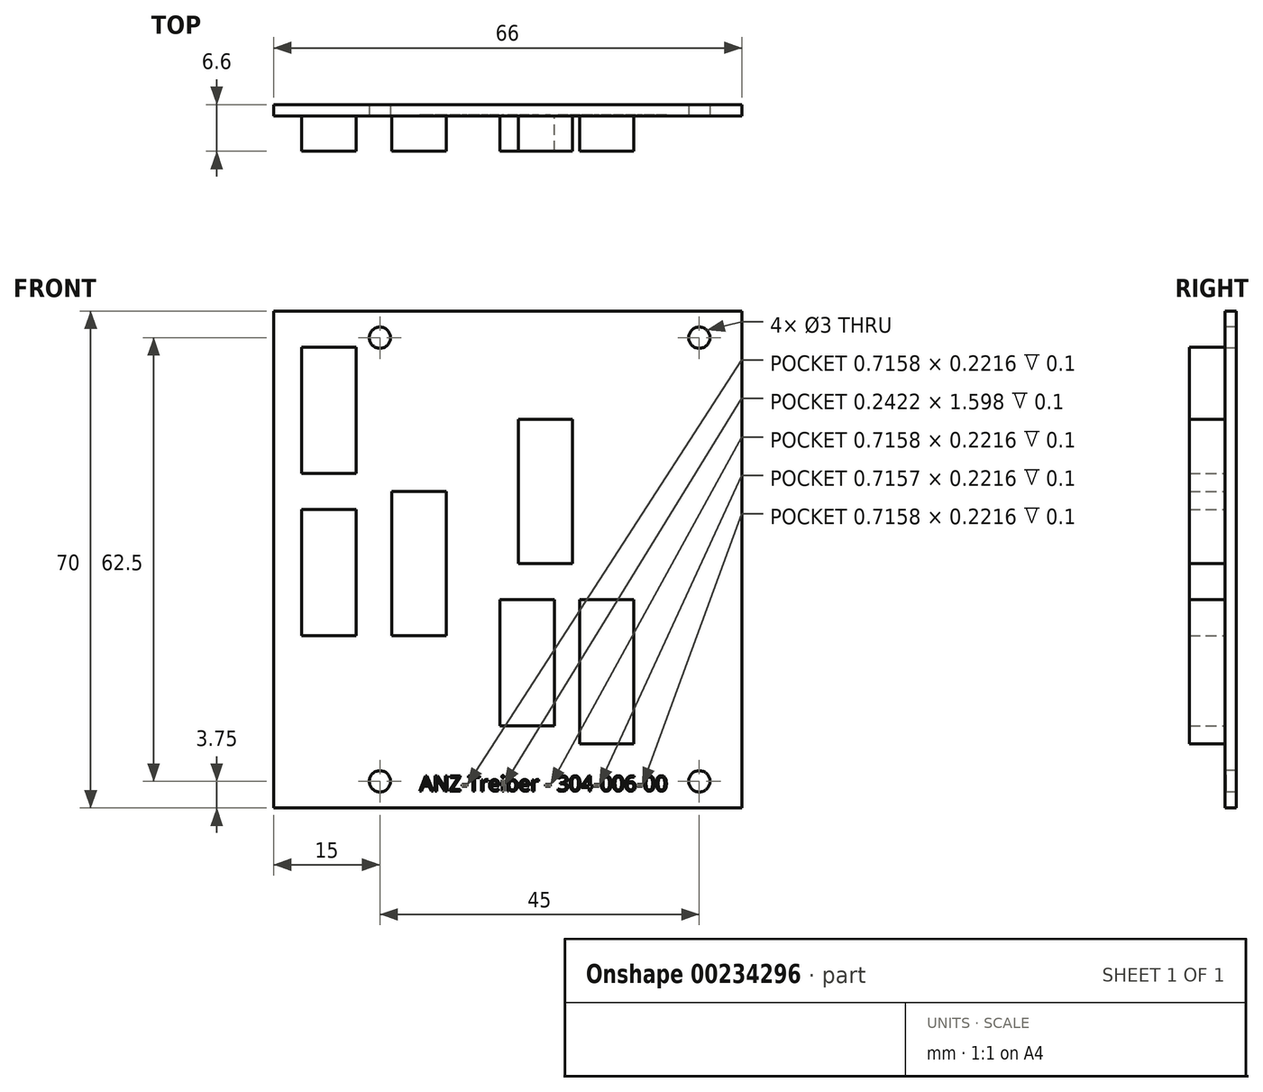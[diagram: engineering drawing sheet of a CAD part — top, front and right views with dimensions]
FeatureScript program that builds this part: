
annotation { "Feature Type Name" : "Feature", "Feature Type Description" : "" }
export const myFeature = defineFeature(function(context is Context, id is Id, definition is map)
    precondition{}
    {
        {
            var Q0;
            Q0=qCreatedBy(makeId("Front.planeOp"),FACE);
            var sketch = newSketch(context, id + "F0", { "sketchPlane" : qUnion([Q0])});
            skLineSegment(sketch, "E0.bottom", {"start": v(33, -35) * mm, "end": v(-33, -35) * mm});
            skLineSegment(sketch, "E0.top", {"start": v(33, 35) * mm, "end": v(-33, 35) * mm});
            skLineSegment(sketch, "E0.left", {"start": v(33, -35) * mm, "end": v(33, 35) * mm});
            skLineSegment(sketch, "E0.right", {"start": v(-33, -35) * mm, "end": v(-33, 35) * mm});
            skPoint(sketch, "E0.middle", {"position": v(0, 0) * mm});
            skCircle(sketch, "E1", {"center": v(-18, 31.25) * mm, "radius": 1.5 * mm});
            skCircle(sketch, "E2", {"center": v(27, 31.25) * mm, "radius": 1.5 * mm});
            skCircle(sketch, "E3", {"center": v(-18, -31.25) * mm, "radius": 1.5 * mm});
            skCircle(sketch, "E4", {"center": v(27, -31.25) * mm, "radius": 1.5 * mm});
            skLineSegment(sketch, "E5.bottom", {"start": v(-29, 29.92) * mm, "end": v(-21.38, 29.92) * mm});
            skLineSegment(sketch, "E5.top", {"start": v(-29, 12.14) * mm, "end": v(-21.38, 12.14) * mm});
            skLineSegment(sketch, "E5.left", {"start": v(-29, 29.92) * mm, "end": v(-29, 12.14) * mm});
            skLineSegment(sketch, "E5.right", {"start": v(-21.38, 29.92) * mm, "end": v(-21.38, 12.14) * mm});
            skLineSegment(sketch, "E6.bottom", {"start": v(-29, 7.06) * mm, "end": v(-21.38, 7.06) * mm});
            skLineSegment(sketch, "E6.top", {"start": v(-29, -10.72) * mm, "end": v(-21.38, -10.72) * mm});
            skLineSegment(sketch, "E6.left", {"start": v(-29, 7.06) * mm, "end": v(-29, -10.72) * mm});
            skLineSegment(sketch, "E6.right", {"start": v(-21.38, 7.06) * mm, "end": v(-21.38, -10.72) * mm});
            skLineSegment(sketch, "E7.bottom", {"start": v(-16.3, 9.6) * mm, "end": v(-8.68, 9.6) * mm});
            skLineSegment(sketch, "E7.top", {"start": v(-16.3, -10.72) * mm, "end": v(-8.68, -10.72) * mm});
            skLineSegment(sketch, "E7.left", {"start": v(-16.3, 9.6) * mm, "end": v(-16.3, -10.72) * mm});
            skLineSegment(sketch, "E7.right", {"start": v(-8.68, 9.6) * mm, "end": v(-8.68, -10.72) * mm});
            skLineSegment(sketch, "E8.bottom", {"start": v(1.48, 19.76) * mm, "end": v(9.1, 19.76) * mm});
            skLineSegment(sketch, "E8.top", {"start": v(1.48, -0.56) * mm, "end": v(9.1, -0.56) * mm});
            skLineSegment(sketch, "E8.left", {"start": v(1.48, 19.76) * mm, "end": v(1.48, -0.56) * mm});
            skLineSegment(sketch, "E8.right", {"start": v(9.1, 19.76) * mm, "end": v(9.1, -0.56) * mm});
            skLineSegment(sketch, "E9.bottom", {"start": v(-1.06, -5.64) * mm, "end": v(6.56, -5.64) * mm});
            skLineSegment(sketch, "E9.top", {"start": v(-1.06, -23.42) * mm, "end": v(6.56, -23.42) * mm});
            skLineSegment(sketch, "E9.left", {"start": v(-1.06, -5.64) * mm, "end": v(-1.06, -23.42) * mm});
            skLineSegment(sketch, "E9.right", {"start": v(6.56, -5.64) * mm, "end": v(6.56, -23.42) * mm});
            skLineSegment(sketch, "E10.bottom", {"start": v(10.14, -5.64) * mm, "end": v(17.76, -5.64) * mm});
            skLineSegment(sketch, "E10.top", {"start": v(10.14, -25.96) * mm, "end": v(17.76, -25.96) * mm});
            skLineSegment(sketch, "E10.left", {"start": v(10.14, -5.64) * mm, "end": v(10.14, -25.96) * mm});
            skLineSegment(sketch, "E10.right", {"start": v(17.76, -5.64) * mm, "end": v(17.76, -25.96) * mm});
            skSolve(sketch);
        }
        {
            var Q0;
            Q0 = qSketchRegion(id + "F0", true);
            var Q1;
            Q1=makeQuery(id+"F0.imprint","IMPRINT",FACE,{"disambiguationData":[TD([[makeQuery(id+"F0.imprint","IMPRINT",EDGE,{"derivedFrom":sQuery(id+"F0.wireOp",EDGE,"E5.bottom")}),-1.0]])]});
            var Q2;
            Q2=makeQuery(id+"F0.imprint","IMPRINT",FACE,{"disambiguationData":[TD([[makeQuery(id+"F0.imprint","IMPRINT",EDGE,{"derivedFrom":sQuery(id+"F0.wireOp",EDGE,"E6.bottom")}),-1.0]])]});
            var Q3;
            Q3=makeQuery(id+"F0.imprint","IMPRINT",FACE,{"disambiguationData":[TD([[makeQuery(id+"F0.imprint","IMPRINT",EDGE,{"derivedFrom":sQuery(id+"F0.wireOp",EDGE,"E7.bottom")}),-1.0]])]});
            var Q4;
            Q4=makeQuery(id+"F0.imprint","IMPRINT",FACE,{"disambiguationData":[TD([[makeQuery(id+"F0.imprint","IMPRINT",EDGE,{"derivedFrom":sQuery(id+"F0.wireOp",EDGE,"E8.bottom")}),-1.0]])]});
            var Q5;
            Q5=makeQuery(id+"F0.imprint","IMPRINT",FACE,{"disambiguationData":[TD([[makeQuery(id+"F0.imprint","IMPRINT",EDGE,{"derivedFrom":sQuery(id+"F0.wireOp",EDGE,"E9.bottom")}),-1.0]])]});
            var Q6;
            Q6=makeQuery(id+"F0.imprint","IMPRINT",FACE,{"disambiguationData":[TD([[makeQuery(id+"F0.imprint","IMPRINT",EDGE,{"derivedFrom":sQuery(id+"F0.wireOp",EDGE,"E10.bottom")}),-1.0]])]});
            extrude(context, id + "F1", {"entities" : qUnion([Q0, Q1, Q2, Q3, Q4, Q5, Q6]), "oppositeDirection" : true, "depth" : 1.6 * mm, "offsetDistance" : 25 * mm});
        }
        {
            var Q0;
            Q0=makeQuery(id+"F1.opExtrude","CAP_FACE",FACE,{"disambiguationData":[OSD([sQuery(id+"F0.wireOp",EDGE,"E0.bottom"),sQuery(id+"F0.wireOp",EDGE,"E0.top"),sQuery(id+"F0.wireOp",EDGE,"E0.left"),sQuery(id+"F0.wireOp",EDGE,"E0.right"),sQuery(id+"F0.wireOp",EDGE,"E1"),sQuery(id+"F0.wireOp",EDGE,"E2"),sQuery(id+"F0.wireOp",EDGE,"E3"),sQuery(id+"F0.wireOp",EDGE,"E4")])],"isStart":true});
            var sketch = newSketch(context, id + "F2", { "sketchPlane" : qUnion([Q0])});
            skText(sketch, "E11", { "text": "ANZ-Treiber - 304-006-00", "fontName": "OpenSans-Regular.ttf"});
            const initialGuessF2  = {"E11": [-0.0124, -0.03262, 1, 0, 0.00215]};
            skSetInitialGuess(sketch, initialGuessF2);
            skSolve(sketch);
        }
        {
            var Q0;
            Q0 = qSketchRegion(id + "F2", true);
            extrude(context, id + "F3", {"entities" : qUnion([Q0]), "operationType" : NewBodyOperationType.REMOVE, "oppositeDirection" : true, "depth" : .1 * mm, "offsetDistance" : 25 * mm});
        }
        {
            var Q0;
            Q0=makeQuery(id+"F0.imprint","IMPRINT",FACE,{"disambiguationData":[TD([[makeQuery(id+"F0.imprint","IMPRINT",EDGE,{"derivedFrom":sQuery(id+"F0.wireOp",EDGE,"E5.bottom")}),-1.0]])]});
            var Q1;
            Q1=makeQuery(id+"F0.imprint","IMPRINT",FACE,{"disambiguationData":[TD([[makeQuery(id+"F0.imprint","IMPRINT",EDGE,{"derivedFrom":sQuery(id+"F0.wireOp",EDGE,"E6.bottom")}),-1.0]])]});
            var Q2;
            Q2=makeQuery(id+"F0.imprint","IMPRINT",FACE,{"disambiguationData":[TD([[makeQuery(id+"F0.imprint","IMPRINT",EDGE,{"derivedFrom":sQuery(id+"F0.wireOp",EDGE,"E7.bottom")}),-1.0]])]});
            var Q3;
            Q3=makeQuery(id+"F0.imprint","IMPRINT",FACE,{"disambiguationData":[TD([[makeQuery(id+"F0.imprint","IMPRINT",EDGE,{"derivedFrom":sQuery(id+"F0.wireOp",EDGE,"E8.bottom")}),-1.0]])]});
            var Q4;
            Q4=makeQuery(id+"F0.imprint","IMPRINT",FACE,{"disambiguationData":[TD([[makeQuery(id+"F0.imprint","IMPRINT",EDGE,{"derivedFrom":sQuery(id+"F0.wireOp",EDGE,"E9.bottom")}),-1.0]])]});
            var Q5;
            Q5=makeQuery(id+"F0.imprint","IMPRINT",FACE,{"disambiguationData":[TD([[makeQuery(id+"F0.imprint","IMPRINT",EDGE,{"derivedFrom":sQuery(id+"F0.wireOp",EDGE,"E10.bottom")}),-1.0]])]});
            extrude(context, id + "F4", {"entities" : qUnion([Q0, Q1, Q2, Q3, Q4, Q5]), "operationType" : NewBodyOperationType.ADD, "depth" : 5 * mm, "offsetDistance" : 25 * mm});
        }
    });
